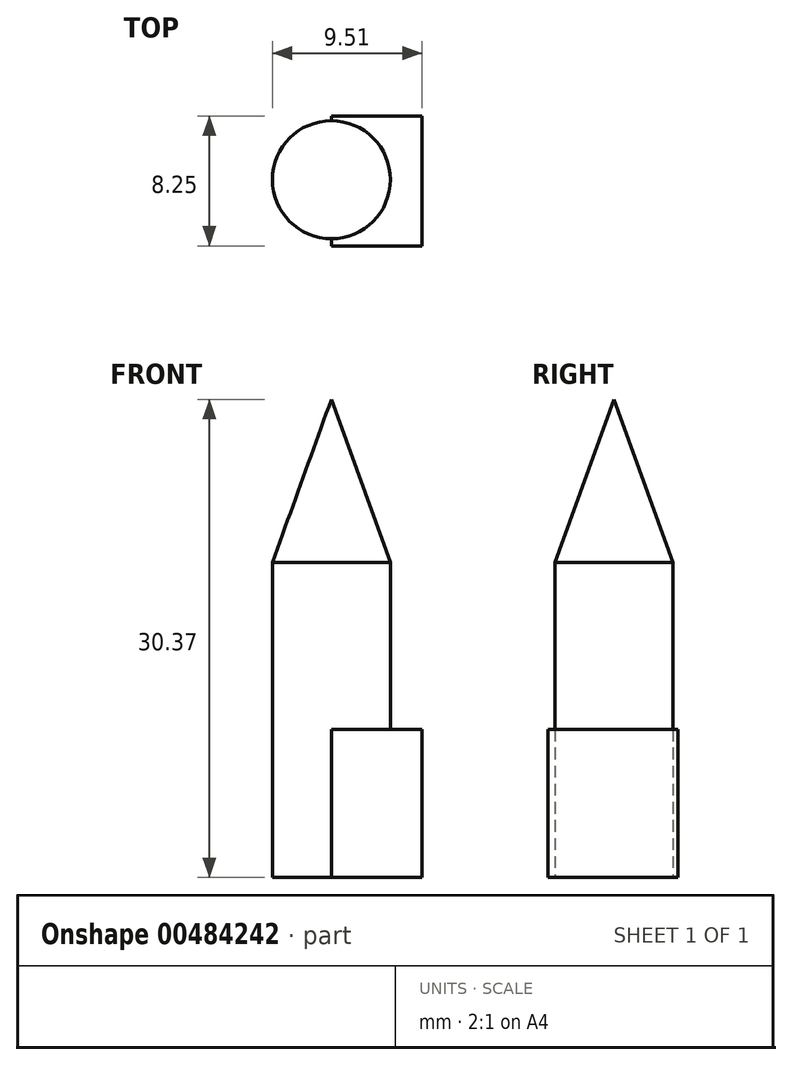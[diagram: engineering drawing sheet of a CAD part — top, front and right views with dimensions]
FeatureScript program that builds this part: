
annotation { "Feature Type Name" : "Feature", "Feature Type Description" : "" }
export const myFeature = defineFeature(function(context is Context, id is Id, definition is map)
    precondition{}
    {
        {
            var Q0;
            Q0=qCreatedBy(makeId("Top.planeOp"),FACE);
            var sketch = newSketch(context, id + "F0", { "sketchPlane" : qUnion([Q0])});
            skCircle(sketch, "E0", {"center": v(0, 0) * mm, "radius": 3.75 * mm});
            skSolve(sketch);
        }
        {
            var Q0;
            Q0=makeQuery(id+"F0.imprint","IMPRINT",FACE,{"disambiguationData":[TD([[makeQuery(id+"F0.imprint","IMPRINT",EDGE,{"derivedFrom":sQuery(id+"F0.wireOp",EDGE,"E0")}),1.0]])]});
            extrude(context, id + "F1", {"entities" : qUnion([Q0]), "depth" : 20 * mm});
        }
        {
            var Q0;
            Q0=qCreatedBy(makeId("Top.planeOp"),FACE);
            var sketch = newSketch(context, id + "F2", { "sketchPlane" : qUnion([Q0])});
            skLineSegment(sketch, "E1.bottom", {"start": v(5.76, 4.05) * mm, "end": v(0, 4.05) * mm});
            skLineSegment(sketch, "E1.top", {"start": v(5.76, -4.2) * mm, "end": v(0, -4.2) * mm});
            skLineSegment(sketch, "E1.left", {"start": v(5.76, 4.05) * mm, "end": v(5.76, -4.2) * mm});
            skLineSegment(sketch, "E1.right", {"start": v(0, 4.05) * mm, "end": v(0, -4.2) * mm});
            skSolve(sketch);
        }
        {
            var Q0;
            Q0=makeQuery(id+"F2.imprint","IMPRINT",FACE,{"disambiguationData":[TD([[makeQuery(id+"F2.imprint","IMPRINT",EDGE,{"derivedFrom":sQuery(id+"F2.wireOp",EDGE,"E1.bottom")}),1.0]])]});
            extrude(context, id + "F3", {"entities" : qUnion([Q0]), "operationType" : NewBodyOperationType.ADD, "depth" : 9.4 * mm});
        }
        {
            var Q0;
            Q0=qCreatedBy(makeId("Front.planeOp"),FACE);
            var sketch = newSketch(context, id + "F4", { "sketchPlane" : qUnion([Q0])});
            skLineSegment(sketch, "E2", {"start": v(0, 20) * mm, "end": v(0, 30.37) * mm});
            skLineSegment(sketch, "E3", {"start": v(0, 20) * mm, "end": v(3.75, 20) * mm});
            skLineSegment(sketch, "E4", {"start": v(3.75, 20) * mm, "end": v(0, 30.37) * mm});
            skSolve(sketch);
        }
        {
            var Q0;
            Q0=qSketchRegion(id+"F4",true);
            var Q1;
            Q1=sQuery(id+"F4.wireOp",EDGE,"E2");
            revolve(context, id + "F5", {"operationType" : NewBodyOperationType.ADD, "entities" : qUnion([Q0]), "axis" : qUnion([Q1]), "revolveType" : RevolveType.FULL});
        }
    });
